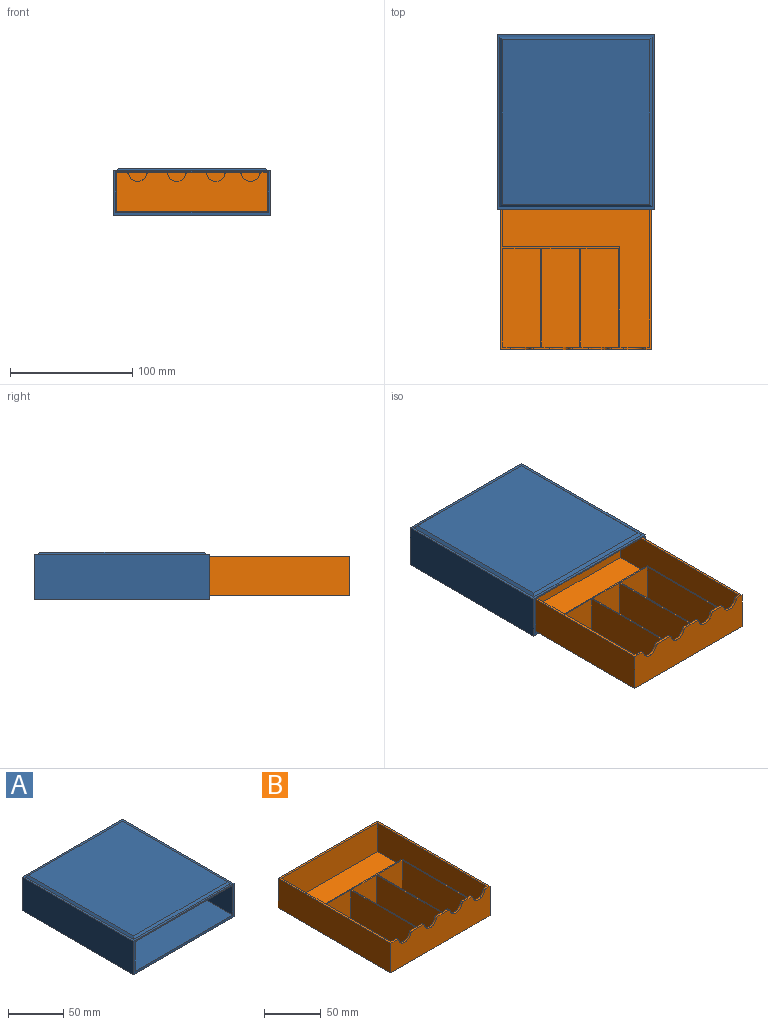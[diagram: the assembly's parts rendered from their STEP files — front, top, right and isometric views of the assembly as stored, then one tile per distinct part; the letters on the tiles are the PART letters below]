
ASSEMBLY  parts=2 mates=1
PART A: 26 faces, bbox 129x143.5x39 mm
  f0: plane 141.5x125mm, normal (0,0,-1), area 905mm2, adj f7,f13,f14,f15,f21,f22,f23,f24
  f1: plane 143.5x129mm, normal (0,0,1), area 1206mm2, adj f4,f5,f6,f7,f17,f18,f19,f20
  f2: plane 141.5x125mm, normal (0,0,1), area 17687.5mm2, adj f7,f13,f14,f15
  f3: plane 143.5x129mm, normal (0,0,-1), area 1074mm2, adj f4,f5,f6,f7,f9,f10,f11,f12
  f4: plane 143.5x37mm, normal (1,0,0), area 5309.5mm2, adj f1,f3,f5,f7
  f5: plane 129x37mm, normal (0,1,0), area 4773mm2, adj f1,f3,f4,f6
  f6: plane 143.5x37mm, normal (-1,0,0), area 5309.5mm2, adj f1,f3,f5,f7
  f7: plane 129x37mm, normal (0,-1,0), area 648mm2, adj f0,f1,f2,f3,f4,f6,f13,f14
  f8: plane 135.5x121mm, normal (0,0,-1), area 16395.5mm2, adj f9,f10,f11,f12
  f9: plane 139.5x2mm, normal (-0.71,0,-0.71), area 388.9mm2, adj f3,f8,f10,f11
  f10: plane 125x2mm, normal (0,0.71,-0.71), area 347.9mm2, adj f3,f8,f9,f12
  f11: plane 125x2mm, normal (0,-0.71,-0.71), area 347.9mm2, adj f3,f8,f9,f12
  f12: plane 139.5x2mm, normal (0.71,0,-0.71), area 388.9mm2, adj f3,f8,f10,f11
  f13: plane 141.5x33mm, normal (-1,0,0), area 4669.5mm2, adj f0,f2,f7,f15
  f14: plane 141.5x33mm, normal (1,0,0), area 4669.5mm2, adj f0,f2,f7,f15
  f15: plane 125x33mm, normal (0,-1,0), area 4125mm2, adj f0,f2,f13,f14
  f16: plane 135x120.5mm, normal (0,0,1), area 16267.5mm2, adj f17,f18,f19,f20
  f17: plane 139x2mm, normal (-0.71,0,0.71), area 387.5mm2, adj f1,f16,f18,f19
  f18: plane 124.5x2mm, normal (0,0.71,0.71), area 346.5mm2, adj f1,f16,f17,f20
  f19: plane 124.5x2mm, normal (0,-0.71,0.71), area 346.5mm2, adj f1,f16,f17,f20
  f20: plane 139x2mm, normal (0.71,0,0.71), area 387.5mm2, adj f1,f16,f18,f19
  f21: plane 137x2mm, normal (0.71,0,-0.71), area 381.8mm2, adj f0,f22,f24,f25
  f22: plane 122.5x2mm, normal (0,0.71,-0.71), area 340.8mm2, adj f0,f21,f23,f25
  f23: plane 137x2mm, normal (-0.71,0,-0.71), area 381.8mm2, adj f0,f22,f24,f25
  f24: plane 122.5x2mm, normal (0,-0.71,-0.71), area 340.8mm2, adj f0,f21,f23,f25
  f25: plane 133x118.5mm, normal (0,0,-1), area 15760.5mm2, adj f21,f22,f23,f24
PART B: 40 faces, bbox 124x141x32 mm
  f0: plane 141x124mm, normal (0,0,1), area 1234.4mm2, adj f1,f2,f3,f4,f5,f6,f7,f8
  f1: plane 81x31mm, normal (1,0,0), area 2511mm2, adj f0,f2,f22,f23
  f2: plane 31x31mm, normal (0,-1,0), area 961mm2, adj f0,f1,f3,f23
  f3: plane 81x31mm, normal (-1,0,0), area 2511mm2, adj f0,f2,f22,f23
  f4: plane 141x32mm, normal (1,0,0), area 4512mm2, adj f0,f5,f18,f27
  f5: plane 124x32mm, normal (0,1,0), area 3968mm2, adj f0,f4,f6,f27
  f6: plane 141x32mm, normal (-1,0,0), area 4512mm2, adj f0,f5,f18,f27
  f7: plane 81x31mm, normal (1,0,0), area 2511mm2, adj f0,f8,f19,f24
  f8: plane 31x31mm, normal (0,-1,0), area 961mm2, adj f0,f7,f9,f24
  f9: plane 81x31mm, normal (-1,0,0), area 2511mm2, adj f0,f8,f19,f24
  f10: plane 31x31mm, normal (0,1,0), area 871.4mm2, adj f0,f11,f20,f25,f31,f36,f37
  f11: plane 81x31mm, normal (1,0,0), area 2511mm2, adj f0,f10,f12,f25
  f12: plane 31x31mm, normal (0,-1,0), area 961mm2, adj f0,f11,f20,f25
  f13: plane 96x31mm, normal (0,1,0), area 2976mm2, adj f0,f14,f21,f26
  f14: plane 55x31mm, normal (1,0,0), area 1705mm2, adj f0,f13,f15,f26
  f15: plane 120x31mm, normal (0,-1,0), area 3720mm2, adj f0,f14,f16,f26
  f16: plane 137x31mm, normal (-1,0,0), area 4247mm2, adj f0,f15,f17,f26
  f17: plane 31x24mm, normal (0,1,0), area 654.4mm2, adj f0,f16,f21,f26,f30,f32,f33
  f18: plane 124x32mm, normal (0,-1,0), area 3609.7mm2, adj f0,f4,f6,f27,f28,f29,f30,f31
  f19: plane 31x31mm, normal (0,1,0), area 871.4mm2, adj f0,f7,f9,f24,f29,f38,f39
  f20: plane 81x31mm, normal (-1,0,0), area 2511mm2, adj f0,f10,f12,f25
  f21: plane 82x31mm, normal (1,0,0), area 2542mm2, adj f0,f13,f17,f26
  f22: plane 31x31mm, normal (0,1,0), area 871.4mm2, adj f0,f1,f3,f23,f28,f34,f35
  f23: plane 81x31mm, normal (0,0,1), area 2511mm2, adj f1,f2,f3,f22
  f24: plane 81x31mm, normal (0,0,1), area 2511mm2, adj f7,f8,f9,f19
  f25: plane 81x31mm, normal (0,0,1), area 2511mm2, adj f10,f11,f12,f20
  f26: plane 137x120mm, normal (0,0,1), area 8568mm2, adj f13,f14,f15,f16,f17,f21
  f27: plane 141x124mm, normal (0,0,-1), area 17484mm2, adj f4,f5,f6,f18
  f28: cylinder r=7.5mm len=14.66mm, axis (0,-1,0), area 40.8mm2, adj f18,f22,f34,f35
  f29: cylinder r=7.5mm len=14.66mm, axis (0,-1,0), area 40.8mm2, adj f18,f19,f38,f39
  f30: cylinder r=7.5mm len=14.66mm, axis (0,-1,0), area 40.8mm2, adj f17,f18,f32,f33
  f31: cylinder r=7.5mm len=14.66mm, axis (0,-1,0), area 40.8mm2, adj f10,f18,f36,f37
  f32: cylinder r=2mm len=2mm, axis (0,-1,0), area 5.4mm2, adj f0,f17,f18,f30
  f33: cylinder r=2mm len=2mm, axis (0,-1,0), area 5.4mm2, adj f0,f17,f18,f30
  f34: cylinder r=2mm len=2mm, axis (0,-1,0), area 5.4mm2, adj f0,f18,f22,f28
  f35: cylinder r=2mm len=2mm, axis (0,-1,0), area 5.4mm2, adj f0,f18,f22,f28
  f36: cylinder r=2mm len=2mm, axis (0,-1,0), area 5.4mm2, adj f0,f10,f18,f31
  f37: cylinder r=2mm len=2mm, axis (0,-1,0), area 5.4mm2, adj f0,f10,f18,f31
  f38: cylinder r=2mm len=2mm, axis (0,-1,0), area 5.4mm2, adj f0,f18,f19,f29
  f39: cylinder r=2mm len=2mm, axis (0,-1,0), area 5.4mm2, adj f0,f18,f19,f29
PLACE A t=(0.01,-0.02,-19.48)mm fixed
PLACE B t=(0.01,-115.77,-15.98)mm
MATE slider A.f15 <-> B.f5  axis (0,-1,0) through (0.01,69.73,0.02)mm
